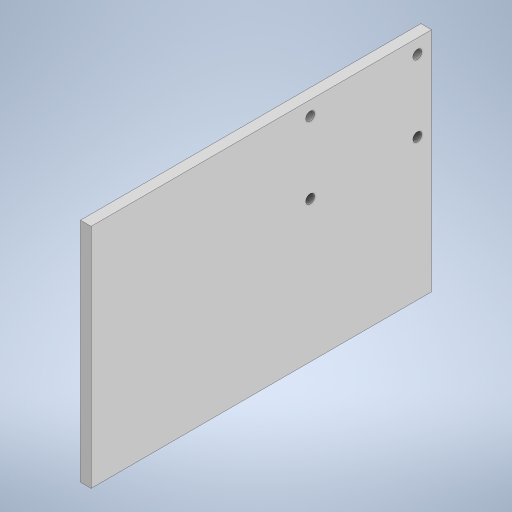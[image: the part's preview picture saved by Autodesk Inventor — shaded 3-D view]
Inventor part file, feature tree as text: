
AUTODESK INVENTOR PART (.ipt)
format: ipt  version: 2024.2 (Build 282272000, 272)  size: 212,992 bytes
history: native  units: in
note: dims shown in document units (in); Inventor stores cm internally (conversion verified against a paired STEP export)
features: extrude x3, sketch x3
ambient origin geometry x8: Origin, YZ Plane, XZ Plane, XY Plane, X Axis, Y Axis, Z Axis, Center Point
bodies: Solid1 (feature_tree)
feature tree (6):
  extrude  "Extrusion1"  Depth=6.0in
  extrude  "Extrusion2"  Depth=0.1875in
  extrude  "Extrusion3"  Depth=0.1875in
  sketch  "Sketch1"  dims[d0=4.0in d1=6.0in]
  sketch  "Sketch3"  dims[d2=0.1875in d3=0.0in d4=1.26in]
  sketch  "Sketch4"  dims[d5=0.157in d6=0.157in d7=0.25in d8=0.25in d10=0.1875in d11=0.0in d12=0.25in d13=1.889in d14=1.889in d15=0.157in d16=0.157in d17=1.0in d18=0.0in]
